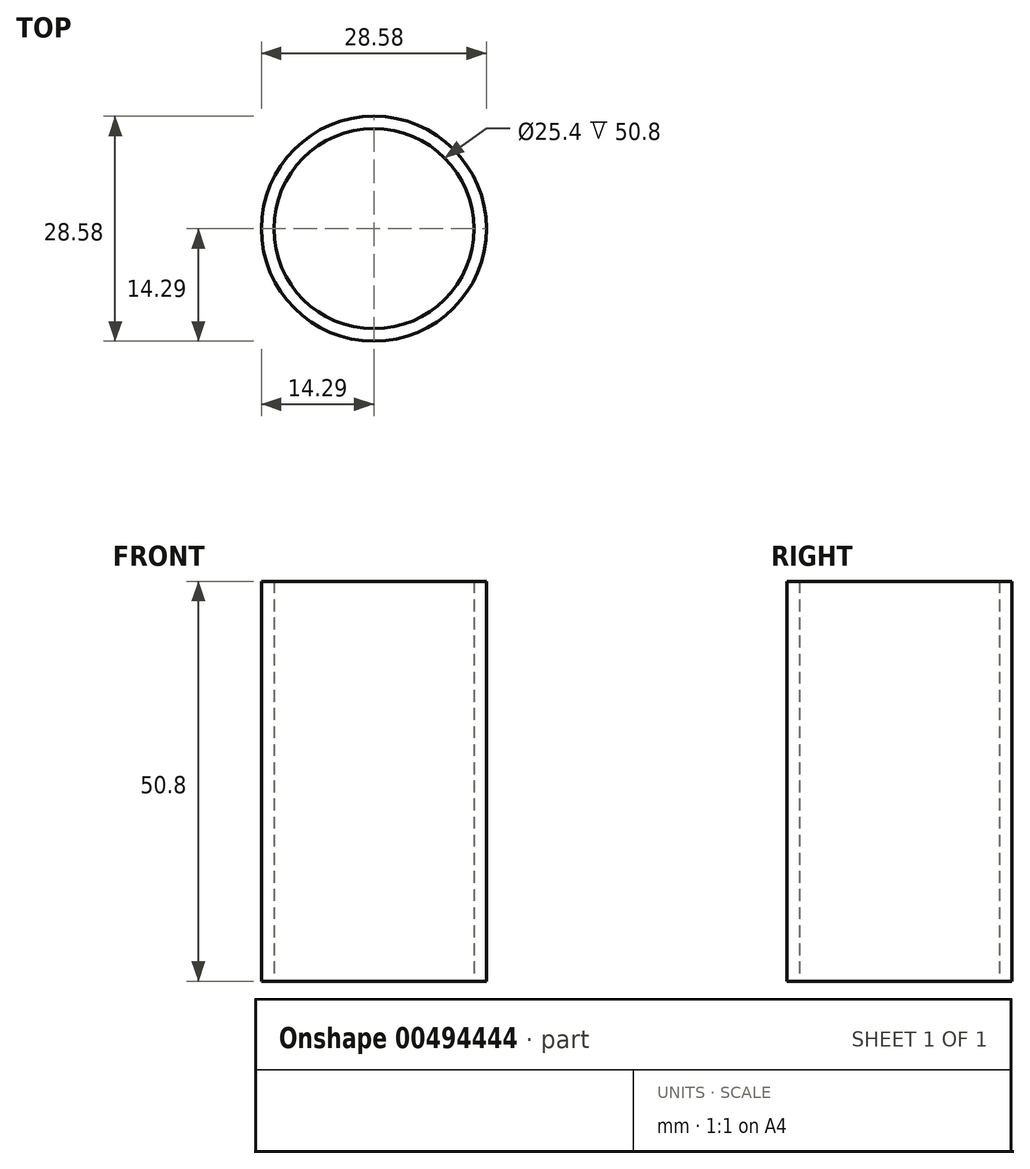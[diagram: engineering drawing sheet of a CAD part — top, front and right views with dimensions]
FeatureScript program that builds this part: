
annotation { "Feature Type Name" : "Feature", "Feature Type Description" : "" }
export const myFeature = defineFeature(function(context is Context, id is Id, definition is map)
    precondition{}
    {
        {
            var Q0;
            Q0=qCreatedBy(makeId("Top.planeOp"),FACE);
            var sketch = newSketch(context, id + "F0", { "sketchPlane" : qUnion([Q0])});
            skCircle(sketch, "E0", {"center": v(0, 0) * mm, "radius": 12.7 * mm});
            skCircle(sketch, "E1", {"center": v(0, 0) * mm, "radius": 14.29 * mm});
            skSolve(sketch);
        }
        {
            var Q0;
            Q0=makeQuery(id+"F0.imprint","IMPRINT",FACE,{"disambiguationData":[TD([[makeQuery(id+"F0.imprint","IMPRINT",EDGE,{"derivedFrom":sQuery(id+"F0.wireOp",EDGE,"E0")}),-1.0]])]});
            extrude(context, id + "F1", {"entities" : qUnion([Q0]), "depth" : 50.8 * mm});
        }
    });
